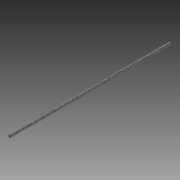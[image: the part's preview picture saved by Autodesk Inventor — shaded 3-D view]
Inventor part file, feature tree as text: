
AUTODESK INVENTOR PART (.ipt)
format: ipt  version: 2013 (Build 170138000, 138)  size: 2,342,400 bytes
history: native  units: in
note: dims shown in document units (in); Inventor stores cm internally (conversion verified against a paired STEP export)
features: sketch x2, extrude x1, helix x1, pattern_circular x1
ambient origin geometry x8: Origin, YZ Plane, XZ Plane, XY Plane, X Axis, Y Axis, Z Axis, Center Point
bodies: Solid1 (feature_tree)
feature tree (5):
  extrude  "Extrusion1"  Depth=24.0in TaperAngle=0.0deg
  helix  "Coil1"  [1 undecoded]
  pattern_circular  "Circular Pattern1"  [2 undecoded]
  sketch  "Sketch1"  dims[d0=0.4463in d2=24.0in d3=0.0in d4=45.0deg]
  sketch  "Sketch2"  dims[d5=0.3335in d7=1.0in d8=24.0in d9=0.3937in d10=0.0in d11=90.0deg d12=90.0deg d13=0.0in d14=0.0in d15=3.1496in d16=360.0deg]
note: 3 required parameter values undecoded (feature->parameter linkage not recoverable at this tier; creation-order binding heuristic only, values carry confidence <= 0.55)
